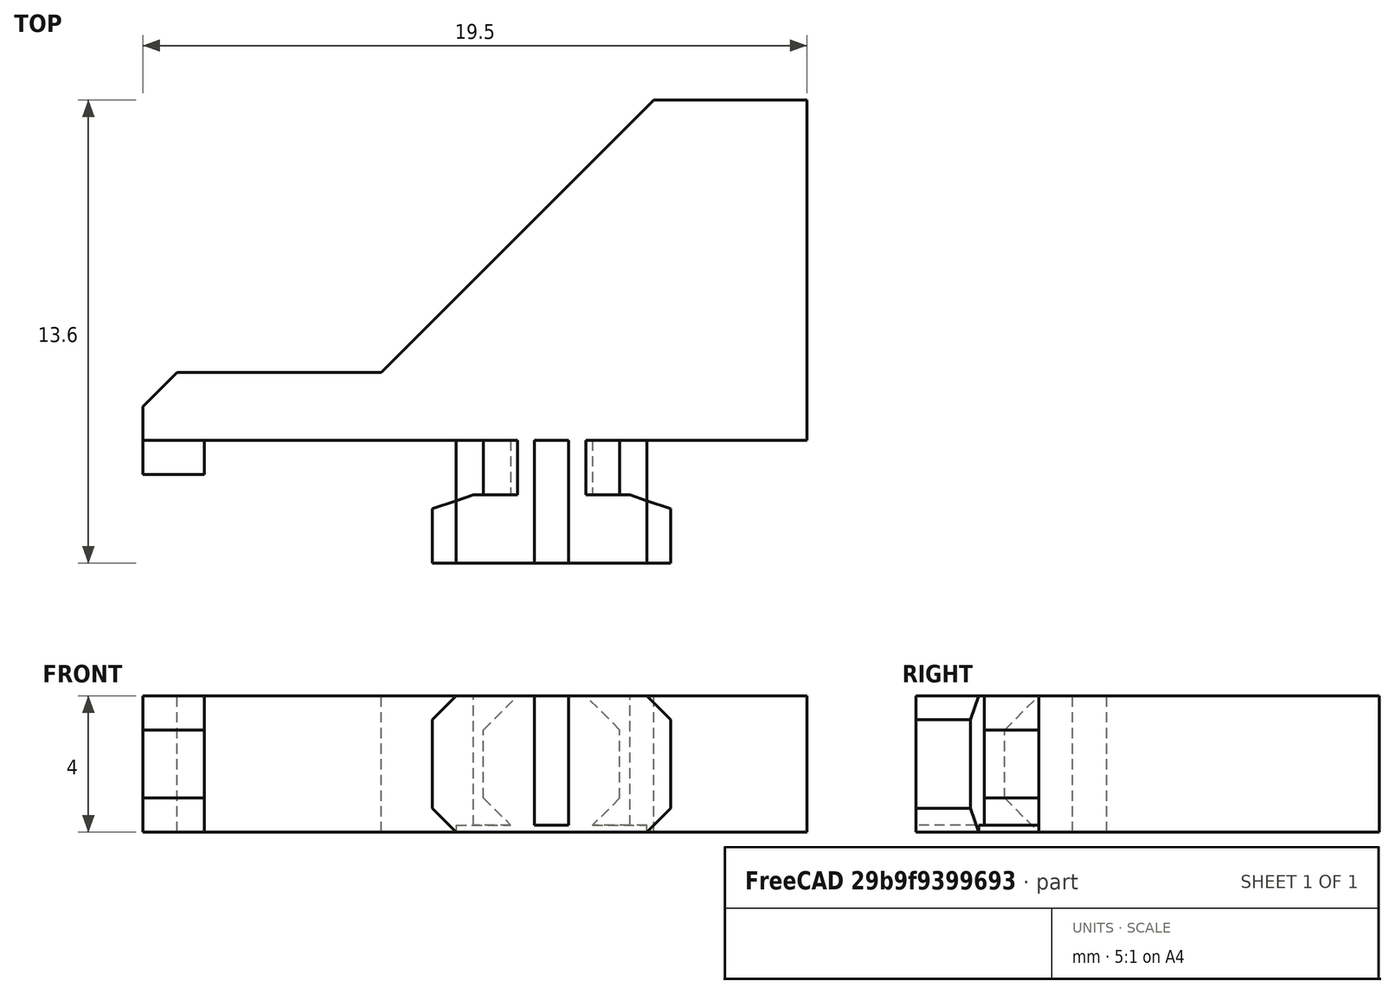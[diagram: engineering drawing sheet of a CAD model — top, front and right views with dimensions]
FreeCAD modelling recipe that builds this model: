
FCSTD DOCUMENT  (FreeCAD 0.18R14555 (Git shallow))
Label: filament-dryer-plate-supporter
License: All rights reserved
LicenseURL: http://en.wikipedia.org/wiki/All_rights_reserved
objects: Part::Box×5, Part::Chamfer×3, Part::Feature×2, Part::MultiFuse×2, Part::Cut×1
note: 13 computed .brp shape members not serialized (recipe doc carries the construction recipe); baked Part::Feature solids carry a one-line shape summary decoded from their .brp

FEATURE [Part::Feature] Fusion008001  label="Fusion006003"
  Placement = pos=(2,0,0) rot=(0,0,1;3.14159rad)
  shape: bbox 7.003 x 7.103 x 4.003 mm, 32 faces (baked)
FEATURE [Part::Box] Box017  label="Cube017"
  AttacherType = Attacher::AttachEngine3D
  Height = 10
  Length = 20
  Placement = pos=(-10,0,0) rot=(0,0,1;0rad)
  Width = 10
FEATURE [Part::Cut] Cut
  Base = -> Fusion008001
  Tool = -> Box017
FEATURE [Part::Box] Box  label="Cube"
  AttacherType = Attacher::AttachEngine3D
  Height = 4
  Length = 12.5
  Placement = pos=(-5,0,0) rot=(0,0,1;0rad)
  Width = 10
FEATURE [Part::Box] Box019  label="Cube019"
  AttacherType = Attacher::AttachEngine3D
  Height = 0.2
  Length = 5.6
  Placement = pos=(-2.8,-3.6,0) rot=(0,0,1;0rad)
  Width = 3.6
FEATURE [Part::Box] Box020  label="Cube020"
  AttacherType = Attacher::AttachEngine3D
  Height = 4
  Length = 1.8
  Placement = pos=(-12,-1,0) rot=(0,0,1;0rad)
  Width = 2
FEATURE [Part::Box] Box021  label="Cube021"
  AttacherType = Attacher::AttachEngine3D
  Height = 4
  Length = 7.5
  Placement = pos=(-12,0,0) rot=(0,0,1;0rad)
  Width = 2
FEATURE [Part::Chamfer] Chamfer001
  Base = -> Box020
  Edges = 2 edges r=1: [Edge9,Edge10]
FEATURE [Part::Chamfer] Chamfer
  Base = -> Box
  Edges = 1 edges r=8: [Edge3]
FEATURE [Part::Chamfer] Chamfer002
  Base = -> Box021
  Edges = 1 edges r=1: [Edge3]
FEATURE [Part::MultiFuse] Fusion
  Shapes = -> [Chamfer002,Cut,Chamfer001,Chamfer]
FEATURE [Part::Feature] Fusion008002  label="Fusion006004"
  shape: bbox 19.5 x 13.6 x 4.003 mm, 35 faces (baked)
FEATURE [Part::MultiFuse] Fusion008003
  Shapes = -> [Fusion008002,Box019]
